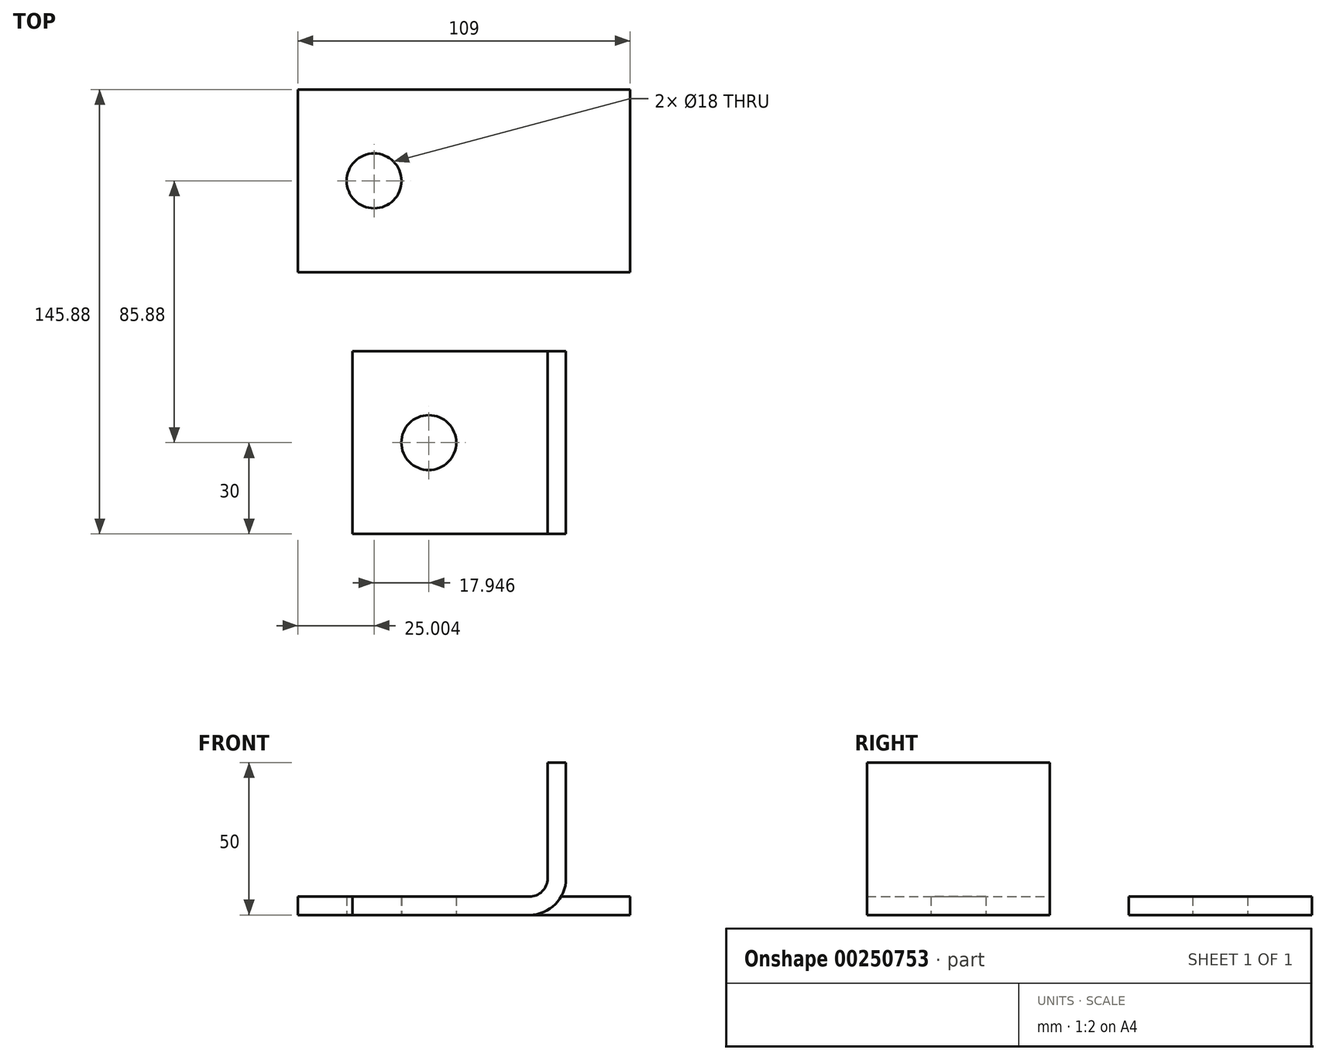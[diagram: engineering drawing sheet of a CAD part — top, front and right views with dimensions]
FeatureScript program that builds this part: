
annotation { "Feature Type Name" : "Feature", "Feature Type Description" : "" }
export const myFeature = defineFeature(function(context is Context, id is Id, definition is map)
    precondition{}
    {
        {
            var Q0;
            Q0=qCreatedBy(makeId("Front.planeOp"),FACE);
            var sketch = newSketch(context, id + "F0", { "sketchPlane" : qUnion([Q0])});
            skLineSegment(sketch, "E0", {"start": v(-70, 0) * mm, "end": v(-12, 0) * mm});
            skLineSegment(sketch, "E1", {"start": v(0, 12) * mm, "end": v(0, 50) * mm});
            skLineSegment(sketch, "E2", {"start": v(0, 50) * mm, "end": v(-6, 50) * mm});
            skLineSegment(sketch, "E3", {"start": v(-6, 50) * mm, "end": v(-6, 12) * mm});
            skLineSegment(sketch, "E4", {"start": v(-12, 6) * mm, "end": v(-70, 6) * mm});
            skLineSegment(sketch, "E5", {"start": v(-70, 6) * mm, "end": v(-70, 0) * mm});
            skPoint(sketch, "E6.visualSharp", {"position": v(0, 0) * mm});
            skPoint(sketch, "E7.visualSharp", {"position": v(-6, 6) * mm});
            skArc(sketch, "E7.filletArc", {"start": v(-12, 6) * mm, "mid": v(-7.76, 7.76) * mm, "end": v(-6, 12) * mm});
            skArc(sketch, "E8.filletArc", {"start": v(-12, 0) * mm, "mid": v(-3.51, 3.51) * mm, "end": v(0, 12) * mm});
            skSolve(sketch);
        }
        {
            var Q0;
            Q0=qSketchRegion(id+"F0",true);
            extrude(context, id + "F1", {"entities" : qUnion([Q0]), "depth" : 60 * mm});
        }
        {
            var Q0;
            Q0=makeQuery(id+"F1.opExtrude","SWEPT_FACE",FACE,{"disambiguationData":[OSD([sQuery(id+"F0.wireOp",EDGE,"E0")])]});
            var sketch = newSketch(context, id + "F2", { "sketchPlane" : qUnion([Q0])});
            skCircle(sketch, "E9", {"center": v(-45, 30) * mm, "radius": 9 * mm});
            skSolve(sketch);
        }
        {
            var Q0;
            Q0=qSketchRegion(id+"F2",true);
            extrude(context, id + "F3", {"entities" : qUnion([Q0]), "operationType" : NewBodyOperationType.REMOVE, "oppositeDirection" : true, "depth" : 25 * mm});
        }
        {
            var Q0;
            Q0=qCreatedBy(makeId("Top.planeOp"),FACE);
            var sketch = newSketch(context, id + "F4", { "sketchPlane" : qUnion([Q0])});
            skLineSegment(sketch, "E10.bottom", {"start": v(-87.95, 25.88) * mm, "end": v(21.05, 25.88) * mm});
            skLineSegment(sketch, "E10.top", {"start": v(-87.95, 85.88) * mm, "end": v(21.05, 85.88) * mm});
            skLineSegment(sketch, "E10.left", {"start": v(-87.95, 25.88) * mm, "end": v(-87.95, 85.88) * mm});
            skLineSegment(sketch, "E10.right", {"start": v(21.05, 25.88) * mm, "end": v(21.05, 85.88) * mm});
            skCircle(sketch, "E11", {"center": v(-62.95, 55.88) * mm, "radius": 9 * mm});
            skSolve(sketch);
        }
        {
            var Q0;
            Q0 = qSketchRegion(id + "F4", true);
            extrude(context, id + "F5", {"entities" : qUnion([Q0]), "depth" : 6 * mm});
        }
    });
